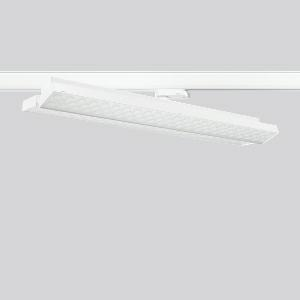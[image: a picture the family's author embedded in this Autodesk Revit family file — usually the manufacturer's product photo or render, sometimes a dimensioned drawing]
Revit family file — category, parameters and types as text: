
# Revit family: tx-move_742162_002_3_76_8ce4
name_source: partatom
category: Lighting Fixtures
units: mm (PartAtom-declared; Revit-internal decimal feet)

## family parameters
Cut with Voids When Loaded = No
Host = Face
Light Source = No
Part Type = Normal
Room Calculation Point = No
Round Connector Dimension = Use Diameter
Shared = No

## types (1)
- MultiLumen 1 (1 x LED Modul 835, 3050 lm, 3500)
    Apparent Load = 41 VA
    CIE Flux Codes = 77 96 99 100 100
    Color Rendering = 80
    Color Temperature = 3500
    Default Elevation = 1800 mm
    Description = Series: TX-MOVE
Multifunctional surface-mounted spotlight for area lighting. Very flat design. Housing: sheet steel, powder-coated. Rotation range: 356°. Swivel range: 90°. Consistent alignment possible with visible tilt scale. High-efficiency LED units with optimum light control thanks to clear plastic (PC) lens optics. Spezielle Mikrostrukturen reduzieren Gelbsaum. Symmetrical light distribution. With adapter for RZB 3-circuit DALI tracks. Suitable for Track on ceiling. MultiLumen: Luminous flux adjustable in 3 steps. Factory setting is the highest luminous flux. Environmentally friendly and resource-saving due to replaceable and recyclable components. 
Colour: traffic white, matt (RAL 9016)
Length: 570 mm
Width: 119 mm
Height: 88 mm
Lamp: LED
Socket: without socket
Colour temperature: 3500K
Colour rendering index (CRI): 80
System power: 41 W
Rated luminous flux: 6100 lm
Luminous efficiency: 149 lm/W
System power 2: 57 W
Rated luminous flux 2: 8300 lm
Luminous efficiency 2: 146 lm/W
System power 3: 73 W
Rated luminous flux 3: 10200 lm
Luminous efficiency 3: 140 lm/W
Control gear: Dimmable EVG, DALI
Protection class: I
Type of protection: IP 20
    Height = 75 mm
    Lamp = 1 x LED Modul 835
    Lamp Light Flux = 3050 lm
    Lamp count = 1
    Length = 569 mm
    Lifetime = 50000 h
    Luminous efficacy = 149 lm/W
    Manufacturer = RZB
    ModVariant = No
    Model = 742162.002.3.76
    Mounting Place = Ceiling
    Mounting Type = Rail mounted
    Number of Poles = 1
    OnlyDefault = Yes
    Power Factor = 1
    Product Name = TX-MOVE
    Product group = Track mounted projectors
    ProductGroupID = 301
    Protection Class = Protection class I
    Protection Degree = IP 20
    RLX_Detail_Level = 1
    RLX_Emergency_Light_Flux = 0 lm
    RLX_Emergency_Type = 0
    RLX_Emergency_Type_DB = No
    RlxData = <blob elided: 31173 chars, md5=07fa7c77>
    Socket = socket
    Standby Power = 0 W
    System Light Flux = 6100 lm
    System Power = 41 W
    Type Comments = MultiLumen 1
    Type Image = 742162.002.jpg
    URL = http://relux.com
    VarID = multilumen_1
    Voltage = 230 V
    Voltage Range = 220-240 V
    Weight = 0.00 kg
    Width = 119 mm

## geometry (parser evidence)
native form markers: Blend x4, Sweep x15
no freeform markers — native parametric forms only
